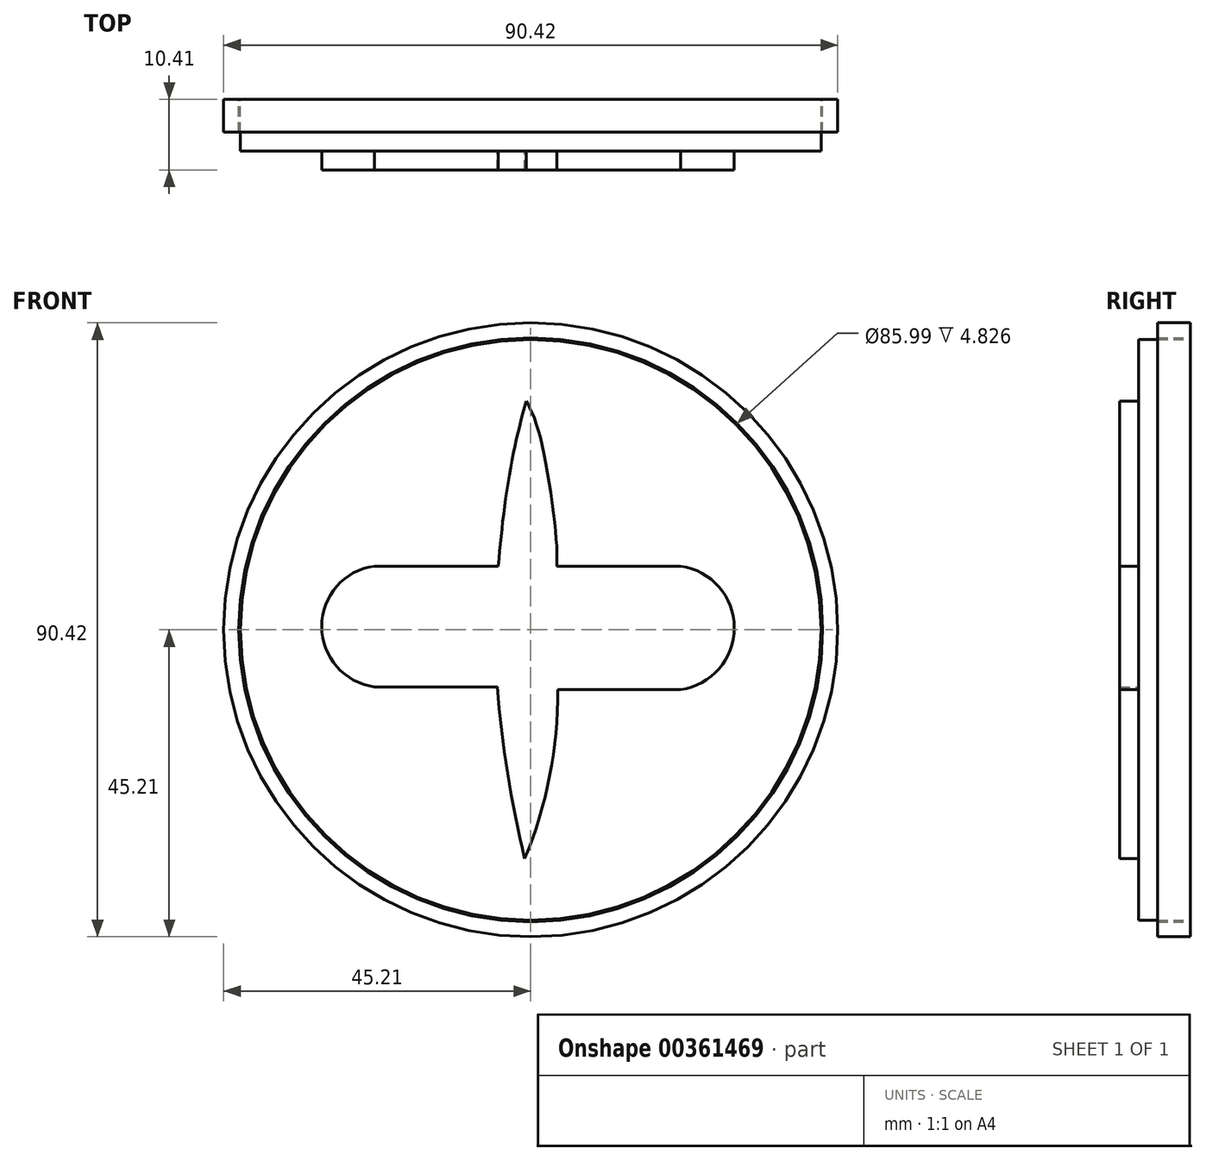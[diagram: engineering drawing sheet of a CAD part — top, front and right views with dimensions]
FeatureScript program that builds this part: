
annotation { "Feature Type Name" : "Feature", "Feature Type Description" : "" }
export const myFeature = defineFeature(function(context is Context, id is Id, definition is map)
    precondition{}
    {
        {
            var Q0;
            Q0=qCreatedBy(makeId("Front.planeOp"),FACE);
            var sketch = newSketch(context, id + "F0", { "sketchPlane" : qUnion([Q0])});
            skCircle(sketch, "E0", {"center": v(0, 0) * mm, "radius": 45.2 * mm});
            skCircle(sketch, "E1", {"center": v(0, 0) * mm, "radius": 43 * mm});
            skSolve(sketch);
        }
        {
            var Q0;
            Q0 = qSketchRegion(id + "F0", true);
            extrude(context, id + "F1", {"entities" : qUnion([Q0]), "depth" : 4.83 * mm});
        }
        {
            var Q0;
            Q0=qCreatedBy(makeId("Front.planeOp"),FACE);
            var sketch = newSketch(context, id + "F2", { "sketchPlane" : qUnion([Q0])});
            skCircle(sketch, "E2", {"center": v(0, 0) * mm, "radius": 42.75 * mm});
            skSolve(sketch);
        }
        {
            var Q0;
            Q0 = qSketchRegion(id + "F2", true);
            extrude(context, id + "F3", {"entities" : qUnion([Q0]), "depth" : 7.62 * mm});
        }
        {
            var Q0;
            Q0=makeQuery(id+"F3.opExtrude","CAP_FACE",FACE,{"disambiguationData":[OSD([sQuery(id+"F2.wireOp",EDGE,"E2")])],"isStart":false});
            var sketch = newSketch(context, id + "F4", { "sketchPlane" : qUnion([Q0])});
            skFitSpline(sketch, "E3", {"points": [v(-0.65, 33.7) * mm, v(-2.33, 27.08) * mm, v(-3.86, 18.1) * mm, v(-4.76, 9.4) * mm], "startDerivative": vector(-5.67, -20.8) * mm, "endDerivative": vector(-2.25, -24.93) * mm});
            skFitSpline(sketch, "E4", {"points": [v(-0.65, 33.7) * mm, v(0.53, 31.2) * mm, v(2.41, 23.6) * mm, v(3.8, 12.66) * mm, v(3.87, 9.4) * mm], "startDerivative": vector(6.83, -12.6) * mm, "endDerivative": vector(-0.21, -14.47) * mm});
            skLineSegment(sketch, "E5", {"start": v(-4.76, 9.4) * mm, "end": v(-23, 9.4) * mm});
            skArc(sketch, "E6", {"start": v(-23, 9.4) * mm, "mid": v(-30.77, 0.5) * mm, "end": v(-23, -8.39) * mm});
            skLineSegment(sketch, "E7", {"start": v(-23, -8.39) * mm, "end": v(-4.94, -8.39) * mm});
            skLineSegment(sketch, "E8", {"start": v(3.87, 9.4) * mm, "end": v(22.06, 9.4) * mm});
            skArc(sketch, "E9", {"start": v(22.06, -8.8) * mm, "mid": v(29.98, 0.3) * mm, "end": v(22.06, 9.4) * mm});
            skLineSegment(sketch, "E10", {"start": v(22.06, -8.8) * mm, "end": v(4, -8.8) * mm});
            skArc(sketch, "E11", {"start": v(-4.94, -8.39) * mm, "mid": v(-3.41, -21.14) * mm, "end": v(-0.88, -33.72) * mm});
            skArc(sketch, "E12", {"start": v(-0.88, -33.72) * mm, "mid": v(2.8, -21.5) * mm, "end": v(4, -8.8) * mm});
            skSolve(sketch);
        }
        {
            var Q0;
            Q0 = qSketchRegion(id + "F4", true);
            extrude(context, id + "F5", {"entities" : qUnion([Q0]), "operationType" : NewBodyOperationType.ADD, "depth" : 2.8 * mm});
        }
    });
